# Revit family: PA601M Citizen Madera
name_source: partatom
category: Mobiliario
units: mm (PartAtom-declared; Revit-internal decimal feet)

## family parameters
Compartido = No
Corte con vacíos al cargar = No
Número OmniClass = 23.40.20.00
Punto de cálculo de habitación = No
Se basa en plano de trabajo = No
Siempre vertical = Sí
Título OmniClass = General Furniture and Specialties

## types (1)
- PA601M Papelera Citizen
    Acabado Papelera = Color Marson
    Accessibilidad = Sí
    Altura = 920 mm  [stored 3.01837 ft]
    Ancho = 546 mm  [stored 1.79134 ft]
    Comentarios de tipo = Estructura de acero con tratamiento Ferrus, proceso protector del hieroo, que garantiza una óptima resistencia a la corrosión.Listones de madera para exterior tratada con Lignus, protector fungicida, insecticida e hidrófugo. Aro de acero zincado para fijar la bolsa.
    Diámetro = 450 mm  [stored 1.47638 ft]
    Fabricante = BENITO
    Ficha tecnica = http://www.benito.com
    Instalación = Anclaje recomenadado, mediante 4 tornillos de expansión. No suministrados
    Material Cubeta = Aro de acero con listones de madera.
    Material estructura = Fundición dúctil
    Modelo = Papelera Citizen Madera
    Referencia = PA601M
    URL = https://www.benito.com
    URL Producto = http://www.benito.com

note: [stored X ft] marks values corroborated as IEEE doubles in the binary element streams (Revit-internal decimal feet)

## geometry (parser evidence)
native form markers: Blend x4
no freeform markers — native parametric forms only
